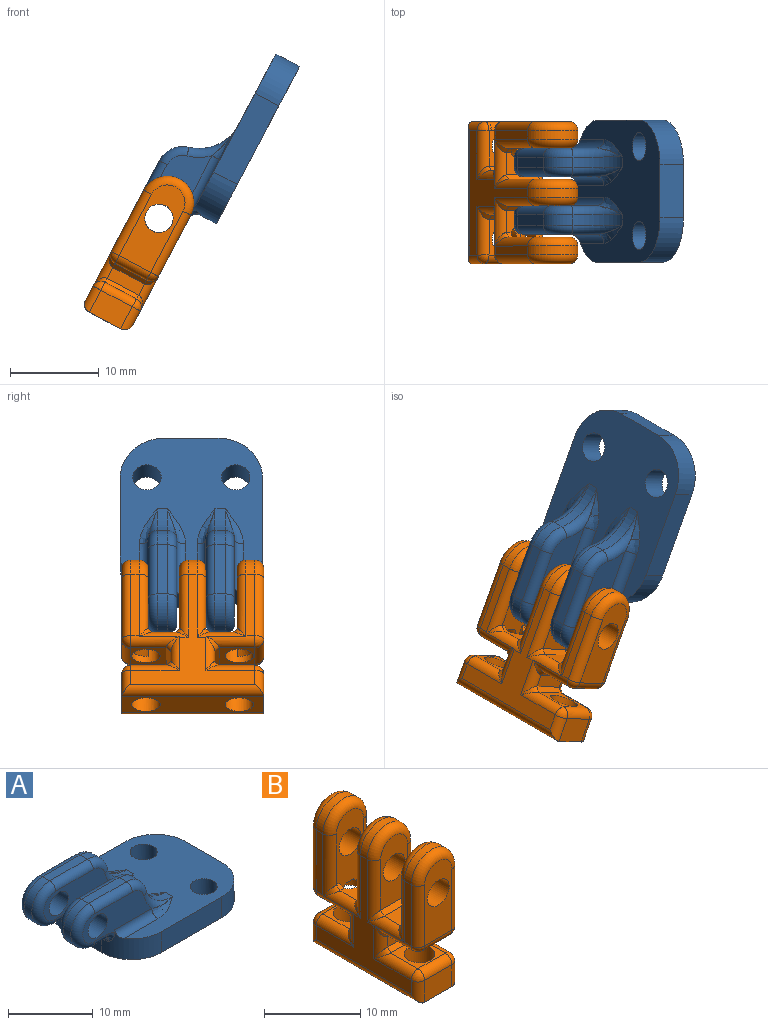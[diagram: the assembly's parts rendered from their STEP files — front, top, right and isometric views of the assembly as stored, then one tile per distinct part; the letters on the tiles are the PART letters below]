
ASSEMBLY  parts=2 mates=1
PART A: 64 faces, bbox 26.7x16.4x9.7 mm
  f0: plane 20.43x16.43mm, normal (0,0,1), area 182.7mm2, adj f1,f2,f3,f4,f18,f19,f20,f21
  f1: plane 6.37x4.37mm, normal (-1,0,0), area 16.9mm2, adj f0,f5,f7,f11,f22,f25,f29,f30
  f2: plane 10x3mm, normal (0,-1,0), area 30mm2, adj f0,f5,f22,f23
  f3: plane 6x3mm, normal (1,0,0), area 18mm2, adj f0,f5,f23,f24
  f4: plane 10x3mm, normal (0,1,0), area 30mm2, adj f0,f5,f24,f25
  f5: plane 20x16mm, normal (0,0,-1), area 282.5mm2, adj f1,f2,f3,f4,f18,f19,f22,f23
  f6: plane 11.53x4.46mm, normal (0,1,0), area 31.8mm2, adj f15,f25,f44,f45,f46,f47,f48,f49
  f7: plane 11.53x4.27mm, normal (0,-1,0), area 31.7mm2, adj f1,f15,f38,f39,f40,f41,f42,f43
  f8: plane 6.25x1.2mm, normal (0,0,1), area 7.5mm2, adj f17,f27,f40,f46
  f9: plane 2.06x1.2mm, normal (0,0,-1), area 2.4mm2, adj f17,f30,f31,f42,f48
  f10: plane 11.53x4.46mm, normal (0,-1,0), area 31.8mm2, adj f14,f22,f50,f51,f52,f53,f54,f55
  f11: plane 11.53x4.27mm, normal (0,1,0), area 31.7mm2, adj f1,f14,f32,f33,f34,f35,f36,f37
  f12: plane 6.25x1.2mm, normal (0,0,1), area 7.5mm2, adj f16,f26,f34,f52
  f13: plane 2.06x1.2mm, normal (0,0,-1), area 2.4mm2, adj f16,f28,f29,f36,f54
  f14: cylinder r=1.6mm len=3.2mm, axis (0,1,0), area 32.2mm2, adj f10,f11
  f15: cylinder r=1.6mm len=3.2mm, axis (0,1,0), area 32.2mm2, adj f6,f7
  f16: cylinder r=3mm len=6mm, axis (0,1,0), area 11.3mm2, adj f12,f13,f35,f53
  f17: cylinder r=3mm len=6mm, axis (0,1,0), area 11.3mm2, adj f8,f9,f41,f47
  f18: cylinder r=1.6mm len=3.2mm, axis (0,0,-1), area 30.2mm2, adj f0,f5
  f19: cylinder r=1.6mm len=3.2mm, axis (0,0,-1), area 30.2mm2, adj f0,f5
  f20: cylinder r=5mm len=4.84mm, axis (0,1,0), area 7.9mm2, adj f0,f26,f32,f50
  f21: cylinder r=5mm len=4.84mm, axis (0,1,0), area 7.9mm2, adj f0,f27,f38,f44
  f22: cylinder r=5mm len=5mm, axis (0,0,1), area 22.5mm2, adj f0,f1,f2,f5,f10,f28,f55,f56
  f23: cylinder r=5mm len=5mm, axis (0,0,-1), area 23.6mm2, adj f0,f2,f3,f5
  f24: cylinder r=5mm len=5mm, axis (0,0,1), area 23.6mm2, adj f0,f3,f4,f5
  f25: cylinder r=5mm len=5mm, axis (0,0,-1), area 22.5mm2, adj f0,f1,f4,f5,f6,f31,f49,f58
  f26: cylinder r=3mm len=2.9mm, axis (0,1,0), area 4.7mm2, adj f12,f20,f33,f51
  f27: cylinder r=3mm len=2.9mm, axis (0,1,0), area 4.7mm2, adj f8,f21,f39,f45
  f28: torus R=6mm, axis (0,0,1), area 1.5mm2, adj f13,f22,f29,f55
  f29: cylinder r=1mm len=1mm, axis (0,1,0), area 0.5mm2, adj f1,f13,f28,f37
  f30: cylinder r=1mm len=1mm, axis (0,1,0), area 0.5mm2, adj f1,f9,f31,f43
  f31: torus R=6mm, axis (0,0,1), area 1.5mm2, adj f9,f25,f30,f49
  f32: torus R=6mm, axis (0,1,0), area 7.4mm2, adj f11,f20,f33,f63
  f33: torus R=2mm, axis (0,1,0), area 5.5mm2, adj f11,f26,f32,f34
  f34: cylinder r=1mm len=6.25mm, axis (1,0,0), area 9.8mm2, adj f11,f12,f33,f35
  f35: torus R=2mm, axis (0,1,0), area 13mm2, adj f11,f16,f34,f36
  f36: cylinder r=1mm len=2mm, axis (-1,0,0), area 3.1mm2, adj f11,f13,f35,f37
  f37: torus R=2mm, axis (0,1,0), area 2.1mm2, adj f1,f11,f29,f36
  f38: torus R=6mm, axis (0,1,0), area 7.4mm2, adj f7,f21,f39,f61
  f39: torus R=2mm, axis (0,1,0), area 5.5mm2, adj f7,f27,f38,f40
  f40: cylinder r=1mm len=6.25mm, axis (-1,0,0), area 9.8mm2, adj f7,f8,f39,f41
  f41: torus R=2mm, axis (0,1,0), area 13mm2, adj f7,f17,f40,f42
  f42: cylinder r=1mm len=2mm, axis (1,0,0), area 3.1mm2, adj f7,f9,f41,f43
  f43: torus R=2mm, axis (0,1,0), area 2.1mm2, adj f1,f7,f30,f42
  f44: torus R=6mm, axis (0,1,0), area 7.4mm2, adj f6,f21,f45,f59
  f45: torus R=2mm, axis (0,1,0), area 5.5mm2, adj f6,f27,f44,f46
  f46: cylinder r=1mm len=6.25mm, axis (1,0,0), area 9.8mm2, adj f6,f8,f45,f47
  f47: torus R=2mm, axis (0,1,0), area 13mm2, adj f6,f17,f46,f48
  f48: cylinder r=1mm len=2.06mm, axis (-1,0,0), area 3.2mm2, adj f6,f9,f47,f49
  f49: bspline ~2.37x2.31mm, area 2.2mm2, adj f6,f25,f31,f48
  f50: torus R=6mm, axis (0,1,0), area 7.4mm2, adj f10,f20,f51,f57
  f51: torus R=2mm, axis (0,1,0), area 5.5mm2, adj f10,f26,f50,f52
  f52: cylinder r=1mm len=6.25mm, axis (-1,0,0), area 9.8mm2, adj f10,f12,f51,f53
  f53: torus R=2mm, axis (0,1,0), area 13mm2, adj f10,f16,f52,f54
  f54: cylinder r=1mm len=2.06mm, axis (1,0,0), area 3.2mm2, adj f10,f13,f53,f55
  f55: bspline ~2.37x2.31mm, area 2.2mm2, adj f10,f22,f28,f54
  f56: cylinder r=1mm len=6.17mm, axis (1,0,0), area 9.3mm2, adj f0,f10,f22,f57
  f57: bspline ~5.15x2mm, area 2.5mm2, adj f0,f50,f56
  f58: cylinder r=1mm len=6.17mm, axis (-1,0,0), area 9.3mm2, adj f0,f6,f25,f59
  f59: bspline ~5.15x2mm, area 2.5mm2, adj f0,f44,f58
  f60: cylinder r=1mm len=6.53mm, axis (1,0,0), area 10.3mm2, adj f0,f1,f7,f61
  f61: bspline ~5.15x2mm, area 2.5mm2, adj f0,f38,f60
  f62: cylinder r=1mm len=6.53mm, axis (-1,0,0), area 10.3mm2, adj f0,f1,f11,f63
  f63: bspline ~5.15x2mm, area 2.5mm2, adj f0,f32,f62
PART B: 115 faces, bbox 6.6x16.1x18.4 mm
  f0: plane 7.8x1mm, normal (-1,0,0), area 7.8mm2, adj f33,f73,f79,f84
  f1: plane 7.8x1mm, normal (-1,0,0), area 7.8mm2, adj f32,f36,f42,f48
  f2: plane 7.8x1mm, normal (1,0,0), area 7.8mm2, adj f33,f78,f81,f85
  f3: plane 7.8x1mm, normal (1,0,0), area 7.8mm2, adj f32,f38,f45,f49
  f4: plane 4x2.5mm, normal (0,0,1), area 8.3mm2, adj f15,f47,f50,f99,f101,f104
  f5: plane 4x2.5mm, normal (0,0,1), area 8.3mm2, adj f10,f74,f77,f106,f108,f111
  f6: plane 9.8x4mm, normal (0,-1,0), area 29.4mm2, adj f29,f35,f36,f37,f38
  f7: plane 9.8x4mm, normal (0,1,0), area 29.4mm2, adj f31,f80,f84,f85,f86
  f8: plane 14x14mm, normal (-1,0,0), area 45.8mm2, adj f34,f41,f47,f51,f53,f58,f60,f62
  f9: plane 14x14mm, normal (1,0,0), area 45.8mm2, adj f34,f46,f50,f52,f55,f59,f61,f64
  f10: cylinder r=1.6mm len=3.2mm, axis (0,0,-1), area 12.8mm2, adj f5,f22,f23,f106,f108,f114
  f11: cylinder r=1.6mm len=3.8mm, axis (0,0,-1), area 38.2mm2, adj f16,f18
  f12: plane 4x2.8mm, normal (0,-1,0), area 11.2mm2, adj f16,f54,f58,f59
  f13: cylinder r=1.6mm len=3.8mm, axis (0,0,-1), area 38.2mm2, adj f16,f21
  f14: plane 4x2.8mm, normal (0,1,0), area 11.2mm2, adj f16,f62,f63,f64
  f15: cylinder r=1.6mm len=3.2mm, axis (0,0,-1), area 12.8mm2, adj f4,f19,f28,f99,f101,f113
  f16: plane 16x4mm, normal (0,0,-1), area 47.9mm2, adj f11,f12,f13,f14,f60,f61
  f17: plane 4x1.4mm, normal (0,-1,0), area 5.6mm2, adj f51,f52,f94,f97
  f18: plane 4x4mm, normal (0,0,1), area 8mm2, adj f11,f53,f54,f55,f94
  f19: plane 4x4mm, normal (0,0,-1), area 8mm2, adj f15,f37,f48,f49,f97
  f20: plane 4x1.4mm, normal (0,1,0), area 5.6mm2, adj f75,f76,f88,f91
  f21: plane 4x4mm, normal (0,0,1), area 8mm2, adj f13,f63,f69,f70,f88
  f22: plane 4x4mm, normal (0,0,-1), area 8mm2, adj f10,f79,f80,f81,f91
  f23: plane 10.14x4.14mm, normal (0,-1,0), area 26.8mm2, adj f10,f24,f31,f72,f73,f78,f106,f108
  f24: plane 1.2x0.85mm, normal (0,0,-1), area 0.9mm2, adj f23,f114
  f25: plane 8.5x4mm, normal (0,-1,0), area 24.2mm2, adj f30,f40,f41,f46,f104
  f26: plane 8.5x4mm, normal (0,1,0), area 24.2mm2, adj f30,f67,f68,f71,f111
  f27: plane 1.2x0.85mm, normal (0,0,-1), area 0.9mm2, adj f28,f113
  f28: plane 10.14x4.14mm, normal (0,1,0), area 26.8mm2, adj f15,f27,f29,f39,f42,f45,f99,f101
  f29: cylinder r=1.6mm len=3.2mm, axis (0,1,0), area 30.2mm2, adj f6,f28
  f30: cylinder r=1.6mm len=3.2mm, axis (0,1,0), area 30.2mm2, adj f25,f26
  f31: cylinder r=1.6mm len=3.2mm, axis (0,1,0), area 30.2mm2, adj f7,f23
  f32: cylinder r=3mm len=6mm, axis (0,-1,0), area 9.4mm2, adj f1,f3,f35,f39
  f33: cylinder r=3mm len=6mm, axis (0,1,0), area 9.4mm2, adj f0,f2,f72,f86
  f34: cylinder r=3mm len=6mm, axis (0,1,0), area 9.4mm2, adj f8,f9,f40,f67
  f35: torus R=2mm, axis (0,1,0), area 13mm2, adj f6,f32,f36,f38
  f36: cylinder r=1mm len=7.8mm, axis (0,0,1), area 12.3mm2, adj f1,f6,f35,f43
  f37: cylinder r=1mm len=4mm, axis (-1,0,0), area 6.3mm2, adj f6,f19,f43,f44
  f38: cylinder r=1mm len=7.8mm, axis (0,0,-1), area 12.3mm2, adj f3,f6,f35,f44
  f39: torus R=2mm, axis (0,1,0), area 13mm2, adj f28,f32,f42,f45
  f40: torus R=2mm, axis (0,1,0), area 13mm2, adj f25,f34,f41,f46
  f41: cylinder r=1mm len=8mm, axis (0,0,1), area 11.4mm2, adj f8,f25,f40,f105
  f42: cylinder r=1mm len=7.88mm, axis (0,0,-1), area 11.1mm2, adj f1,f28,f39,f48,f100
  f43: sphere r=1mm, area 1.6mm2, adj f36,f37,f48
  f44: sphere r=1mm, area 1.6mm2, adj f37,f38,f49
  f45: cylinder r=1mm len=7.88mm, axis (0,0,1), area 11.1mm2, adj f3,f28,f39,f49,f102
  f46: cylinder r=1mm len=8mm, axis (0,0,-1), area 11.4mm2, adj f9,f25,f40,f103
  f47: cylinder r=1mm len=5.35mm, axis (0,1,0), area 5.2mm2, adj f4,f8,f48,f51,f96,f100,f105
  f48: cylinder r=1mm len=5.35mm, axis (0,-1,0), area 6.7mm2, adj f1,f19,f42,f43,f47,f96,f100
  f49: cylinder r=1mm len=5.35mm, axis (0,1,0), area 6.7mm2, adj f3,f19,f44,f45,f50,f98,f102
  f50: cylinder r=1mm len=5.35mm, axis (0,-1,0), area 5.2mm2, adj f4,f9,f49,f52,f98,f102,f103
  f51: cylinder r=1mm len=4.28mm, axis (0,0,1), area 3.9mm2, adj f8,f17,f47,f93,f96
  f52: cylinder r=1mm len=4.28mm, axis (0,0,-1), area 3.9mm2, adj f9,f17,f50,f95,f98
  f53: cylinder r=1mm len=5.5mm, axis (0,1,0), area 7.5mm2, adj f8,f18,f56,f93
  f54: cylinder r=1mm len=4mm, axis (1,0,0), area 6.3mm2, adj f12,f18,f56,f57
  f55: cylinder r=1mm len=5.5mm, axis (0,-1,0), area 7.5mm2, adj f9,f18,f57,f95
  f56: sphere r=1mm, area 1.6mm2, adj f53,f54,f58
  f57: sphere r=1mm, area 1.6mm2, adj f54,f55,f59
  f58: cylinder r=1mm len=2.8mm, axis (0,0,1), area 3.6mm2, adj f8,f12,f56,f60
  f59: cylinder r=1mm len=2.8mm, axis (0,0,-1), area 3.6mm2, adj f9,f12,f57,f61
  f60: cylinder r=1mm len=16mm, axis (0,-1,0), area 23.6mm2, adj f8,f16,f58,f62
  f61: cylinder r=1mm len=16mm, axis (0,1,0), area 23.6mm2, adj f9,f16,f59,f64
  f62: cylinder r=1mm len=2.8mm, axis (0,0,-1), area 3.6mm2, adj f8,f14,f60,f65
  f63: cylinder r=1mm len=4mm, axis (1,0,0), area 6.3mm2, adj f14,f21,f65,f66
  f64: cylinder r=1mm len=2.8mm, axis (0,0,1), area 3.6mm2, adj f9,f14,f61,f66
  f65: sphere r=1mm, area 2.1mm2, adj f62,f63,f69
  f66: sphere r=1mm, area 1mm2, adj f63,f64,f70
  f67: torus R=2mm, axis (0,1,0), area 13mm2, adj f26,f34,f68,f71
  f68: cylinder r=1mm len=8mm, axis (0,0,-1), area 11.4mm2, adj f8,f26,f67,f112
  f69: cylinder r=1mm len=5.5mm, axis (0,1,0), area 7.5mm2, adj f8,f21,f65,f87
  f70: cylinder r=1mm len=5.5mm, axis (0,-1,0), area 7.5mm2, adj f9,f21,f66,f89
  f71: cylinder r=1mm len=8mm, axis (0,0,1), area 11.4mm2, adj f9,f26,f67,f110
  f72: torus R=2mm, axis (0,-1,0), area 13mm2, adj f23,f33,f73,f78
  f73: cylinder r=1mm len=7.88mm, axis (0,0,-1), area 11.1mm2, adj f0,f23,f72,f79,f107
  f74: cylinder r=1mm len=5.35mm, axis (0,1,0), area 5.2mm2, adj f5,f8,f75,f79,f90,f107,f112
  f75: cylinder r=1mm len=4.28mm, axis (0,0,-1), area 3.9mm2, adj f8,f20,f74,f87,f90
  f76: cylinder r=1mm len=4.28mm, axis (0,0,1), area 3.9mm2, adj f9,f20,f77,f89,f92
  f77: cylinder r=1mm len=5.35mm, axis (0,-1,0), area 5.2mm2, adj f5,f9,f76,f81,f92,f109,f110
  f78: cylinder r=1mm len=7.88mm, axis (0,0,1), area 11.1mm2, adj f2,f23,f72,f81,f109
  f79: cylinder r=1mm len=5.35mm, axis (0,-1,0), area 6.7mm2, adj f0,f22,f73,f74,f82,f90,f107
  f80: cylinder r=1mm len=4mm, axis (-1,0,0), area 6.3mm2, adj f7,f22,f82,f83
  f81: cylinder r=1mm len=5.35mm, axis (0,1,0), area 6.7mm2, adj f2,f22,f77,f78,f83,f92,f109
  f82: sphere r=1mm, area 2.1mm2, adj f79,f80,f84
  f83: sphere r=1mm, area 1mm2, adj f80,f81,f85
  f84: cylinder r=1mm len=7.8mm, axis (0,0,-1), area 12.3mm2, adj f0,f7,f82,f86
  f85: cylinder r=1mm len=7.8mm, axis (0,0,1), area 12.3mm2, adj f2,f7,f83,f86
  f86: torus R=2mm, axis (0,1,0), area 13mm2, adj f7,f33,f84,f85
  f87: bspline ~1.52x1.52mm, area 0.5mm2, adj f69,f75,f88
  f88: plane 4x0.5mm, normal (0,0.71,0.71), area 2.8mm2, adj f20,f21,f87,f89
  f89: bspline ~1.52x1.52mm, area 0.5mm2, adj f70,f76,f88
  f90: bspline ~1.52x1.52mm, area 0.9mm2, adj f74,f75,f79,f91
  f91: plane 4x0.5mm, normal (0,0.71,-0.71), area 2.8mm2, adj f20,f22,f90,f92
  f92: bspline ~1.52x1.52mm, area 0.9mm2, adj f76,f77,f81,f91
  f93: bspline ~1.52x1.52mm, area 0.5mm2, adj f51,f53,f94
  f94: plane 4x0.5mm, normal (0,-0.71,0.71), area 2.8mm2, adj f17,f18,f93,f95
  f95: bspline ~1.52x1.52mm, area 0.5mm2, adj f52,f55,f94
  f96: bspline ~1.52x1.52mm, area 0.9mm2, adj f47,f48,f51,f97
  f97: plane 4x0.5mm, normal (0,-0.71,-0.71), area 2.8mm2, adj f17,f19,f96,f98
  f98: bspline ~1.52x1.52mm, area 0.9mm2, adj f49,f50,f52,f97
  f99: plane 0.6x0.51mm, normal (0,0.71,0.71), area 0.3mm2, adj f4,f15,f28,f100
  f100: bspline ~1.52x1.52mm, area 0.9mm2, adj f42,f47,f48,f99
  f101: plane 0.6x0.51mm, normal (0,0.71,0.71), area 0.3mm2, adj f4,f15,f28,f102
  f102: bspline ~1.52x1.52mm, area 0.9mm2, adj f45,f49,f50,f101
  f103: bspline ~1.52x1.52mm, area 0.5mm2, adj f46,f50,f104
  f104: plane 4x0.5mm, normal (0,-0.71,0.71), area 2.8mm2, adj f4,f25,f103,f105
  f105: bspline ~1.52x1.52mm, area 0.5mm2, adj f41,f47,f104
  f106: plane 0.6x0.51mm, normal (0,-0.71,0.71), area 0.3mm2, adj f5,f10,f23,f107
  f107: bspline ~1.52x1.52mm, area 0.9mm2, adj f73,f74,f79,f106
  f108: plane 0.6x0.51mm, normal (0,-0.71,0.71), area 0.3mm2, adj f5,f10,f23,f109
  f109: bspline ~1.52x1.52mm, area 0.9mm2, adj f77,f78,f81,f108
  f110: bspline ~1.52x1.52mm, area 0.5mm2, adj f71,f77,f111
  f111: plane 4x0.5mm, normal (0,0.71,0.71), area 2.8mm2, adj f5,f26,f110,f112
  f112: bspline ~1.52x1.52mm, area 0.5mm2, adj f68,f74,f111
  f113: cone r=1.6mm half-angle=45deg, axis (0,0,-1), area 5.7mm2, adj f15,f27,f28
  f114: cone r=1.6mm half-angle=45deg, axis (0,0,-1), area 5.7mm2, adj f10,f23,f24
PLACE A rot(axis=(0,-1,0),62.1deg) t=(7.04,-3.21,17.03)mm
PLACE B rot(axis=(0,1,0),27.9deg) t=(-10.18,-3.36,-2.71)mm
MATE fastened A.f14 <-> B.f29  axis (0,1,0) through (-4.1,1.64,8.78)mm
